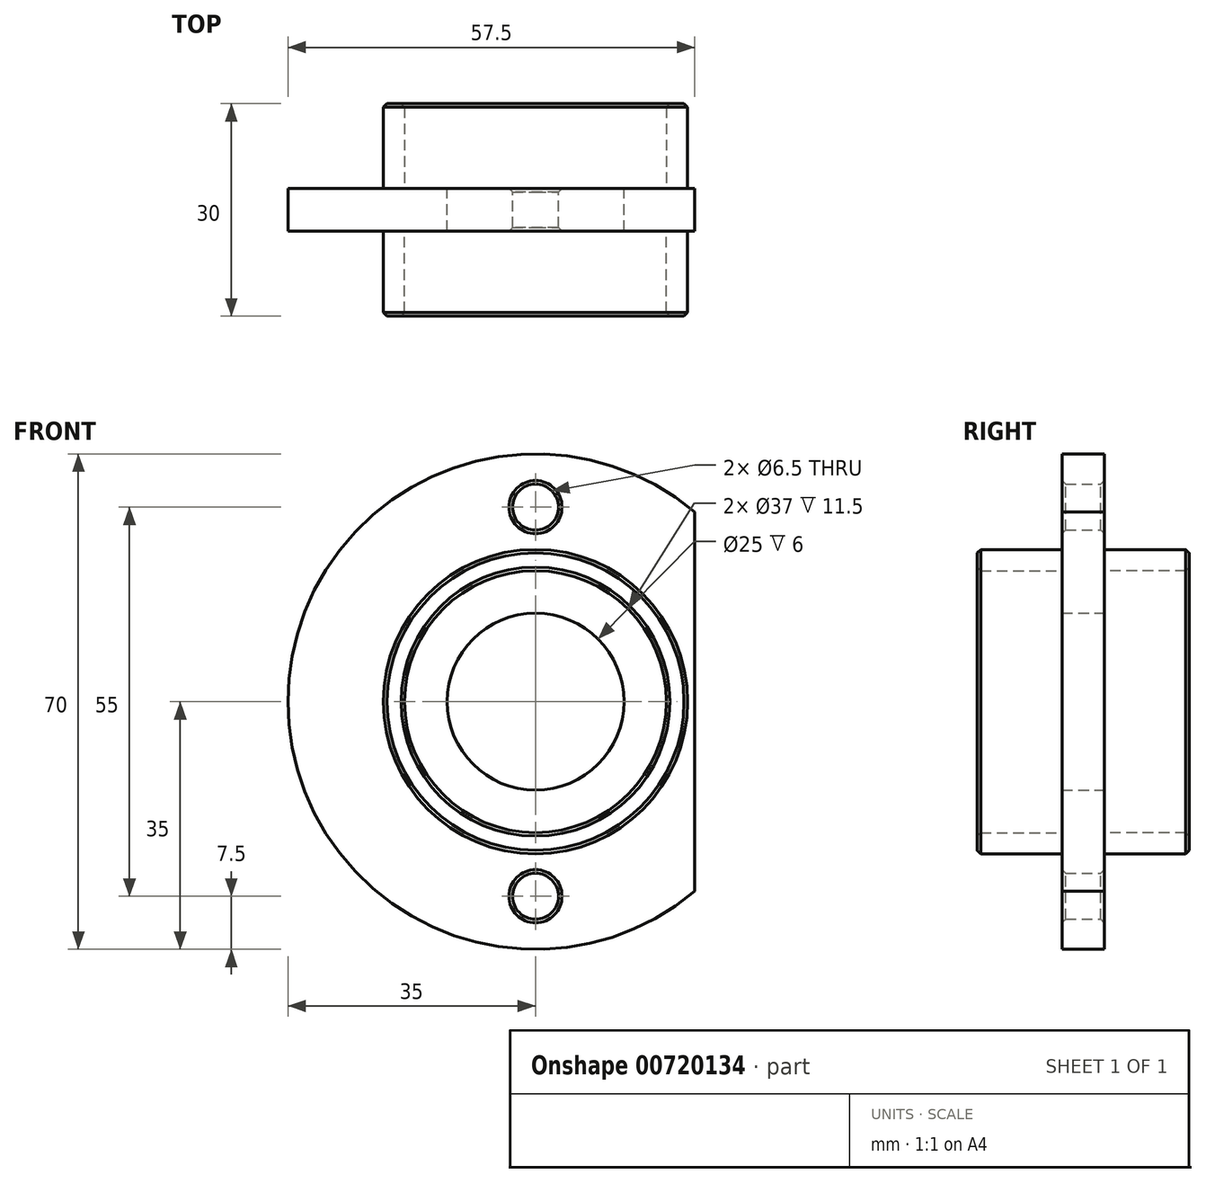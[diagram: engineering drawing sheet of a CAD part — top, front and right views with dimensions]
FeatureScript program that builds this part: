
annotation { "Feature Type Name" : "Feature", "Feature Type Description" : "" }
export const myFeature = defineFeature(function(context is Context, id is Id, definition is map)
    precondition{}
    {
        {
            var Q0;
            Q0=qCreatedBy(makeId("Front.planeOp"),FACE);
            var sketch = newSketch(context, id + "F0", { "sketchPlane" : qUnion([Q0])});
            skArc(sketch, "E0", {"start": v(22.5, 26.8) * mm, "mid": v(-35, 0) * mm, "end": v(22.5, -26.8) * mm});
            skCircle(sketch, "E1", {"center": v(0, 0) * mm, "radius": 12.5 * mm});
            skCircle(sketch, "E2", {"center": v(0, 27.5) * mm, "radius": 3.25 * mm});
            skCircle(sketch, "E3", {"center": v(0, -27.5) * mm, "radius": 3.25 * mm});
            skLineSegment(sketch, "E4", {"start": v(-35, 0) * mm, "end": v(-35, 42.33) * mm});
            skLineSegment(sketch, "E5.0", {"start": v(22.5, -26.8) * mm, "end": v(22.5, 26.8) * mm});
            skSolve(sketch);
        }
        {
            var Q0;
            Q0=makeQuery(id+"F0.imprint","IMPRINT",FACE,{"disambiguationData":[TD([[makeQuery(id+"F0.imprint","IMPRINT",EDGE,{"derivedFrom":sQuery(id+"F0.wireOp",EDGE,"E0")}),1.0]])]});
            extrude(context, id + "F1", {"entities" : qUnion([Q0]), "depth" : 6 * mm, "offsetDistance" : 25 * mm});
        }
        {
            var Q0;
            Q0=makeQuery(id+"F1.opExtrude","CAP_FACE",FACE,{"disambiguationData":[OSD([sQuery(id+"F0.wireOp",EDGE,"E0"),sQuery(id+"F0.wireOp",EDGE,"E1"),sQuery(id+"F0.wireOp",EDGE,"E2"),sQuery(id+"F0.wireOp",EDGE,"E3"),sQuery(id+"F0.wireOp",EDGE,"E5.0")])],"isStart":true});
            var sketch = newSketch(context, id + "F2", { "sketchPlane" : qUnion([Q0])});
            skCircle(sketch, "E6", {"center": v(0, 0) * mm, "radius": 21.5 * mm});
            skCircle(sketch, "E7", {"center": v(0, 0) * mm, "radius": 18.5 * mm});
            skSolve(sketch);
        }
        {
            var Q0;
            Q0=makeQuery(id+"F2.imprint","IMPRINT",FACE,{"disambiguationData":[TD([[makeQuery(id+"F2.imprint","IMPRINT",EDGE,{"derivedFrom":sQuery(id+"F2.wireOp",EDGE,"E6")}),1.0]])]});
            extrude(context, id + "F3", {"entities" : qUnion([Q0]), "operationType" : NewBodyOperationType.ADD, "depth" : 12 * mm, "offsetDistance" : 25 * mm});
        }
        {
            var Q0;
            Q0=makeQuery(id+"F1.opExtrude","CAP_FACE",FACE,{"disambiguationData":[OSD([sQuery(id+"F0.wireOp",EDGE,"E0"),sQuery(id+"F0.wireOp",EDGE,"E1"),sQuery(id+"F0.wireOp",EDGE,"E2"),sQuery(id+"F0.wireOp",EDGE,"E3"),sQuery(id+"F0.wireOp",EDGE,"E5.0")])],"isStart":false});
            var sketch = newSketch(context, id + "F4", { "sketchPlane" : qUnion([Q0])});
            skCircle(sketch, "E8", {"center": v(0, 0) * mm, "radius": 21.5 * mm});
            skCircle(sketch, "E9", {"center": v(0, 0) * mm, "radius": 18.5 * mm});
            skSolve(sketch);
        }
        {
            var Q0;
            Q0=makeQuery(id+"F4.imprint","IMPRINT",FACE,{"disambiguationData":[TD([[makeQuery(id+"F4.imprint","IMPRINT",EDGE,{"derivedFrom":sQuery(id+"F4.wireOp",EDGE,"E8")}),1.0]])]});
            extrude(context, id + "F5", {"entities" : qUnion([Q0]), "operationType" : NewBodyOperationType.ADD, "depth" : 12 * mm, "offsetDistance" : 25 * mm});
        }
        {
            var Q0;
            Q0=makeQuery(id+"F1.opExtrude","CAP_EDGE",EDGE,{"disambiguationData":[OSD([sQuery(id+"F0.wireOp",EDGE,"E2")])],"isStart":false});
            var Q1;
            Q1=makeQuery(id+"F1.opExtrude","CAP_EDGE",EDGE,{"disambiguationData":[OSD([sQuery(id+"F0.wireOp",EDGE,"E2")])],"isStart":true});
            var Q2;
            Q2=makeQuery(id+"F1.opExtrude","CAP_EDGE",EDGE,{"disambiguationData":[OSD([sQuery(id+"F0.wireOp",EDGE,"E3")])],"isStart":false});
            var Q3;
            Q3=makeQuery(id+"F1.opExtrude","CAP_EDGE",EDGE,{"disambiguationData":[OSD([sQuery(id+"F0.wireOp",EDGE,"E3")])],"isStart":true});
            var Q4;
            Q4=makeQuery(id+"F5.opExtrude","CAP_EDGE",EDGE,{"disambiguationData":[OSD([sQuery(id+"F4.wireOp",EDGE,"E9")])],"isStart":false});
            var Q5;
            Q5=makeQuery(id+"F5.opExtrude","CAP_EDGE",EDGE,{"disambiguationData":[OSD([sQuery(id+"F4.wireOp",EDGE,"E8")])],"isStart":false});
            var Q6;
            Q6=makeQuery(id+"F3.opExtrude","CAP_EDGE",EDGE,{"disambiguationData":[OSD([sQuery(id+"F2.wireOp",EDGE,"E6")])],"isStart":false});
            var Q7;
            Q7=makeQuery(id+"F3.opExtrude","CAP_EDGE",EDGE,{"disambiguationData":[OSD([sQuery(id+"F2.wireOp",EDGE,"E7")])],"isStart":false});
            chamfer(context, id + "F6", {"entities" : qUnion([Q0, Q1, Q2, Q3, Q4, Q5, Q6, Q7]), "width" : .5 * mm, "tangentPropagation" : true});
        }
    });
